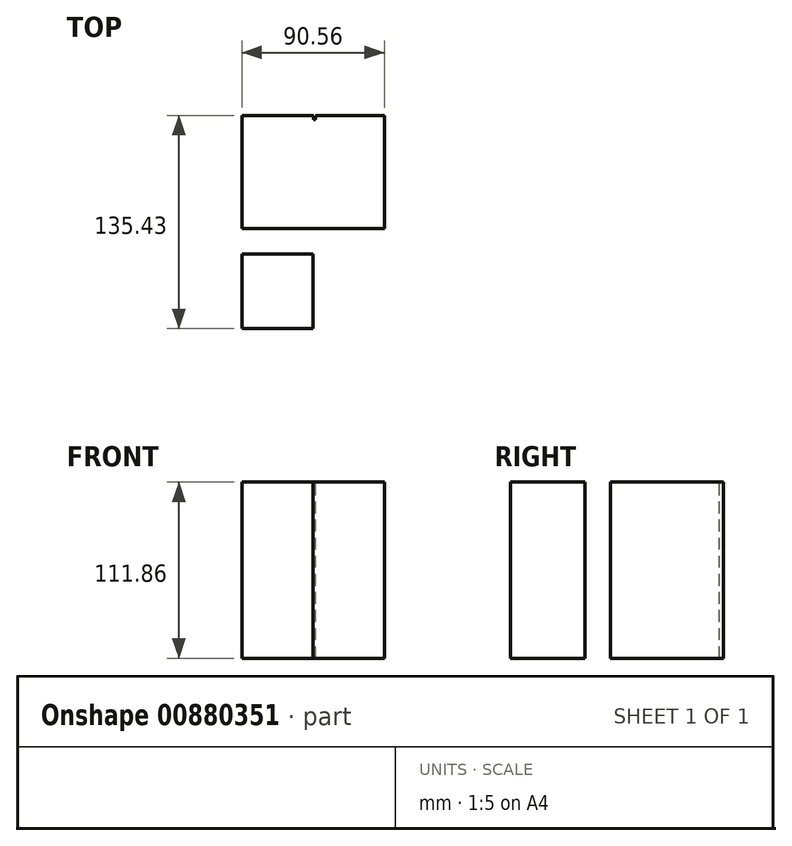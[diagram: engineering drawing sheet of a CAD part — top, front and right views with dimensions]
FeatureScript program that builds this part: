
annotation { "Feature Type Name" : "Feature", "Feature Type Description" : "" }
export const myFeature = defineFeature(function(context is Context, id is Id, definition is map)
    precondition{}
    {
        {
            var Q0;
            Q0=qCreatedBy(makeId("Top.planeOp"),FACE);
            var sketch = newSketch(context, id + "F0", { "sketchPlane" : qUnion([Q0])});
            skLineSegment(sketch, "E0.bottom", {"start": v(22.66, 85.53) * mm, "end": v(24.14, 85.53) * mm});
            skLineSegment(sketch, "E0.top", {"start": v(22.66, 88.2) * mm, "end": v(24.14, 88.2) * mm});
            skLineSegment(sketch, "E0.left", {"start": v(22.66, 85.53) * mm, "end": v(22.66, 88.2) * mm});
            skLineSegment(sketch, "E0.right", {"start": v(24.14, 85.53) * mm, "end": v(24.14, 88.2) * mm});
            skLineSegment(sketch, "E1.bottom", {"start": v(67.76, 88.2) * mm, "end": v(-22.8, 88.2) * mm});
            skLineSegment(sketch, "E1.top", {"start": v(67.76, 16.4) * mm, "end": v(-22.8, 16.4) * mm});
            skLineSegment(sketch, "E1.left", {"start": v(67.76, 88.2) * mm, "end": v(67.76, 16.4) * mm});
            skLineSegment(sketch, "E1.right", {"start": v(-22.8, 88.2) * mm, "end": v(-22.8, 16.4) * mm});
            skPoint(sketch, "E2.oppositeSnap0", {"position": v(22.48, 16.4) * mm});
            skLineSegment(sketch, "E2.bottom", {"start": v(-22.8, 0) * mm, "end": v(22.48, 0) * mm});
            skLineSegment(sketch, "E2.top", {"start": v(-22.8, -47.23) * mm, "end": v(22.48, -47.23) * mm});
            skLineSegment(sketch, "E2.left", {"start": v(-22.8, 0) * mm, "end": v(-22.8, -47.23) * mm});
            skLineSegment(sketch, "E2.right", {"start": v(22.48, 0) * mm, "end": v(22.48, -47.23) * mm});
            skSolve(sketch);
        }
        {
            var Q0;
            Q0=makeQuery(id+"F0.imprint","IMPRINT",FACE,{"disambiguationData":[TD([[makeQuery(id+"F0.imprint","IMPRINT",EDGE,{"derivedFrom":sQuery(id+"F0.wireOp",EDGE,"E2.bottom")}),-1.0]])]});
            var Q1;
            Q1=makeQuery(id+"F0.imprint","IMPRINT",FACE,{"disambiguationData":[TD([[makeQuery(id+"F0.imprint","IMPRINT",EDGE,{"derivedFrom":sQuery(id+"F0.wireOp",EDGE,"E0.bottom")}),-1.0]])]});
            extrude(context, id + "F1", {"entities" : qUnion([Q0, Q1]), "oppositeDirection" : true, "depth" : 111.86 * mm, "offsetDistance" : 25.4 * mm});
        }
    });
